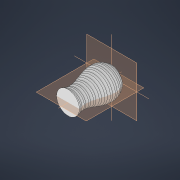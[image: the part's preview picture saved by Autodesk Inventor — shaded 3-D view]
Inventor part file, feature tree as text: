
AUTODESK INVENTOR PART (.ipt)
format: ipt  version: 2021 (Build 250183000, 183)  size: 1,579,520 bytes
history: native  units: mm
features: sketch x6, extrude x2, other x2, revolve x1, plane x1, sweep x1, helix x1
ambient origin geometry x8: Origin, YZ Plane, XZ Plane, XY Plane, X Axis, Y Axis, Z Axis, Center Point
bodies: Body1 (feature_tree), Body2 (feature_tree)
feature tree (14):
  revolve  "Revolution2"  Angle=90.0deg
  plane  "Work Plane1"
  sweep  "Sweep3"
  extrude  "Extrusion7"  Depth=80.0mm
  extrude  "Extrusion8"  Depth=20.0mm
  sketch  "Sketch1"  dims[d37=240.0mm d52=90.0deg]
  other  "Srf4"
  sketch  "3D Sketch3"
  sketch  "Sketch19"  dims[d74=150.0mm d75=80.0mm]
  sketch  "Sketch24"  dims[d76=65.0mm d78=130.0mm d79=20.0mm]
  sketch  "Sketch25"  dims[d80=-20.0mm d89=100.0mm d90=20.0mm d91=240.0mm d92=40.0mm d93=0.0mm d94=90.0deg d95=90.0deg d96=0.0mm d97=0.0mm d99=0.0mm d100=0.0mm d107=20.0mm d108=20.0mm d109=1.0mm d122=20.0mm d123=200.0mm d124=20.0mm d125=0.0mm d126=200.0mm d127=20.0mm d128=0.0mm d129=34.0mm d130=27.0mm d29=0.5mm d30=0.872665mm d31=0.5mm d32=0.872665mm d110=0.5mm d111=0.872665mm d112=0.5mm d113=0.872665mm]
  helix  "Coil3"  [1 undecoded]
  sketch  "Sketch18"  dims[d71=30.0mm d73=240.0mm]
  other  "3D Intersection3"
note: 1 required parameter value undecoded (feature->parameter linkage not recoverable at this tier; creation-order binding heuristic only, values carry confidence <= 0.55)
